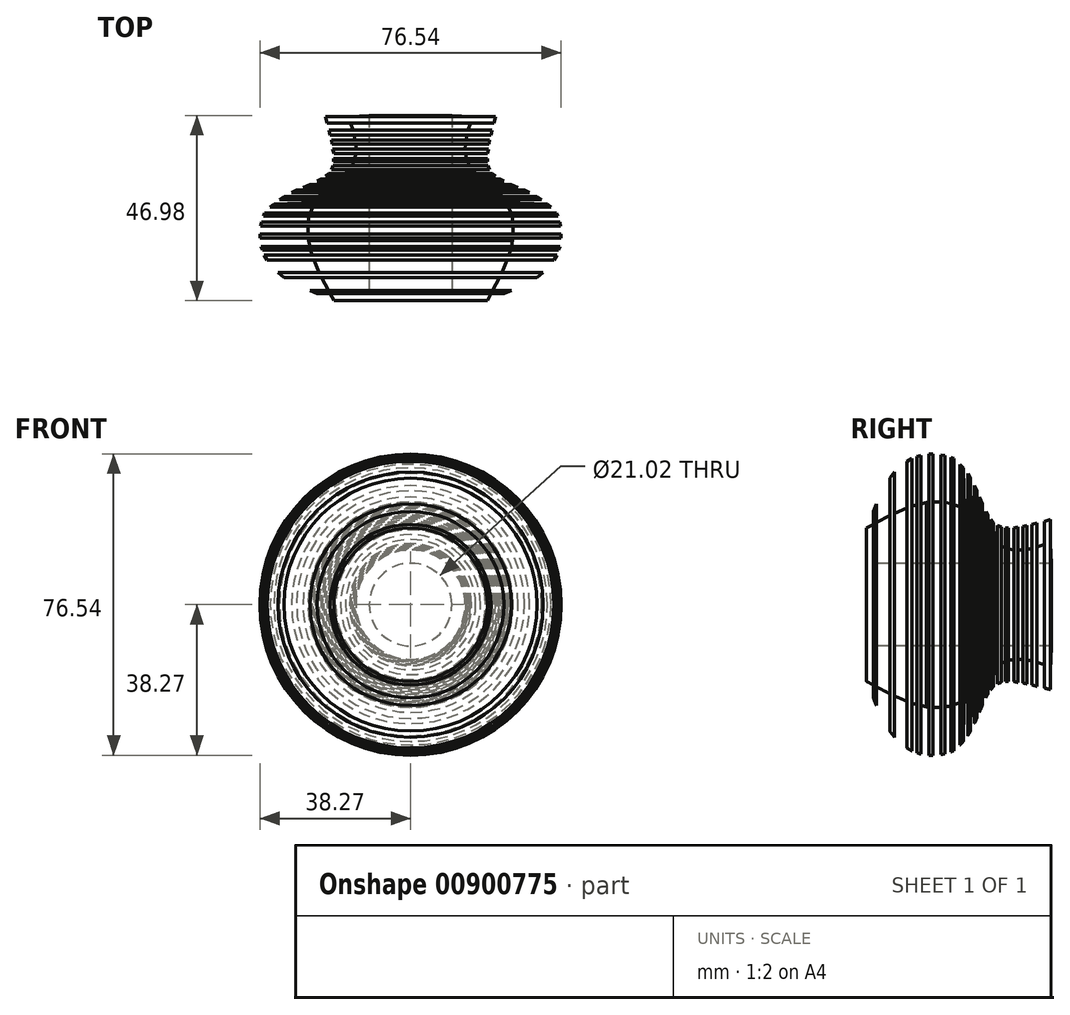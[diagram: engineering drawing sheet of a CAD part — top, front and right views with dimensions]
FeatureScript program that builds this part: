
annotation { "Feature Type Name" : "Feature", "Feature Type Description" : "" }
export const myFeature = defineFeature(function(context is Context, id is Id, definition is map)
    precondition{}
    {
        {
            var Q0;
            Q0=qCreatedBy(makeId("Top.planeOp"),FACE);
            var sketch = newSketch(context, id + "F0", { "sketchPlane" : qUnion([Q0])});
            skLineSegment(sketch, "E0", {"start": v(20.4, 1.74) * mm, "end": v(23.7, 1.74) * mm});
            skLineSegment(sketch, "E1", {"start": v(23.7, 1.74) * mm, "end": v(25.6, 2.49) * mm});
            skLineSegment(sketch, "E2", {"start": v(25.6, 2.49) * mm, "end": v(20.85, 2.49) * mm});
            skLineSegment(sketch, "E3", {"start": v(20.85, 2.49) * mm, "end": v(22.63, 5.9) * mm});
            skLineSegment(sketch, "E4", {"start": v(22.63, 5.9) * mm, "end": v(32.13, 5.9) * mm});
            skLineSegment(sketch, "E5", {"start": v(32.13, 5.9) * mm, "end": v(33.7, 7.16) * mm});
            skLineSegment(sketch, "E6", {"start": v(33.7, 7.16) * mm, "end": v(23.22, 7.16) * mm});
            skLineSegment(sketch, "E7", {"start": v(23.22, 7.16) * mm, "end": v(24.56, 10.32) * mm});
            skLineSegment(sketch, "E8", {"start": v(24.56, 10.32) * mm, "end": v(36.44, 10.32) * mm});
            skLineSegment(sketch, "E9", {"start": v(36.44, 10.32) * mm, "end": v(37.18, 11.5) * mm});
            skLineSegment(sketch, "E10", {"start": v(37.18, 11.5) * mm, "end": v(25, 11.5) * mm});
            skLineSegment(sketch, "E11", {"start": v(25, 11.5) * mm, "end": v(25.42, 12.8) * mm});
            skLineSegment(sketch, "E12", {"start": v(25.42, 12.8) * mm, "end": v(37.62, 12.8) * mm});
            skLineSegment(sketch, "E13", {"start": v(37.62, 12.8) * mm, "end": v(37.94, 13.76) * mm});
            skLineSegment(sketch, "E14", {"start": v(37.94, 13.76) * mm, "end": v(25.6, 13.76) * mm});
            skLineSegment(sketch, "E15", {"start": v(25.6, 13.76) * mm, "end": v(25.96, 15.26) * mm});
            skLineSegment(sketch, "E16", {"start": v(25.96, 15.26) * mm, "end": v(25.96, 15.91) * mm});
            skLineSegment(sketch, "E17", {"start": v(25.96, 15.91) * mm, "end": v(38.27, 15.91) * mm});
            skLineSegment(sketch, "E18", {"start": v(38.27, 15.91) * mm, "end": v(38.27, 16.87) * mm});
            skLineSegment(sketch, "E19", {"start": v(38.27, 16.87) * mm, "end": v(26.08, 16.87) * mm});
            skLineSegment(sketch, "E20", {"start": v(26.08, 16.87) * mm, "end": v(26.08, 18.87) * mm});
            skLineSegment(sketch, "E21", {"start": v(26.08, 18.87) * mm, "end": v(38.09, 18.87) * mm});
            skLineSegment(sketch, "E22", {"start": v(38.09, 19.42) * mm, "end": v(37.9, 19.9) * mm});
            skLineSegment(sketch, "E23", {"start": v(37.9, 19.9) * mm, "end": v(38.09, 18.87) * mm});
            skLineSegment(sketch, "E24", {"start": v(38.07, 19.44) * mm, "end": v(38.07, 19.03) * mm});
            skLineSegment(sketch, "E25", {"start": v(38.07, 19.03) * mm, "end": v(37.9, 19.9) * mm});
            skLineSegment(sketch, "E26", {"start": v(25.98, 19.9) * mm, "end": v(37.9, 19.9) * mm});
            skLineSegment(sketch, "E27", {"start": v(25.98, 19.9) * mm, "end": v(25.74, 21.44) * mm});
            skLineSegment(sketch, "E28", {"start": v(25.74, 21.44) * mm, "end": v(37.4, 21.44) * mm});
            skLineSegment(sketch, "E29", {"start": v(37.4, 21.44) * mm, "end": v(37.08, 22.23) * mm});
            skLineSegment(sketch, "E30", {"start": v(37.08, 22.23) * mm, "end": v(25.45, 22.23) * mm});
            skLineSegment(sketch, "E31", {"start": v(25.45, 22.23) * mm, "end": v(24.77, 23.99) * mm});
            skLineSegment(sketch, "E32", {"start": v(24.77, 23.99) * mm, "end": v(35.66, 23.78) * mm});
            skLineSegment(sketch, "E33", {"start": v(35.66, 23.78) * mm, "end": v(34.74, 24.57) * mm});
            skLineSegment(sketch, "E34", {"start": v(34.74, 24.57) * mm, "end": v(24.32, 24.84) * mm});
            skLineSegment(sketch, "E35", {"start": v(24.32, 24.84) * mm, "end": v(23.7, 25.9) * mm});
            skLineSegment(sketch, "E36", {"start": v(23.7, 25.9) * mm, "end": v(33.28, 25.7) * mm});
            skLineSegment(sketch, "E37", {"start": v(33.28, 25.7) * mm, "end": v(32.16, 26.4) * mm});
            skLineSegment(sketch, "E38", {"start": v(32.16, 26.4) * mm, "end": v(23.23, 26.57) * mm});
            skLineSegment(sketch, "E39", {"start": v(23.23, 26.57) * mm, "end": v(22.44, 27.55) * mm});
            skLineSegment(sketch, "E40", {"start": v(22.44, 27.55) * mm, "end": v(30.23, 27.4) * mm});
            skLineSegment(sketch, "E41", {"start": v(30.23, 27.4) * mm, "end": v(28.93, 28.02) * mm});
            skLineSegment(sketch, "E42", {"start": v(28.93, 28.02) * mm, "end": v(22.05, 28.15) * mm});
            skLineSegment(sketch, "E43", {"start": v(22.05, 28.15) * mm, "end": v(21.24, 28.92) * mm});
            skLineSegment(sketch, "E44", {"start": v(21.24, 28.92) * mm, "end": v(27.35, 28.67) * mm});
            skLineSegment(sketch, "E45", {"start": v(27.35, 28.67) * mm, "end": v(25.54, 29.45) * mm});
            skLineSegment(sketch, "E46", {"start": v(25.54, 29.45) * mm, "end": v(20.56, 29.55) * mm});
            skLineSegment(sketch, "E47", {"start": v(20.56, 29.55) * mm, "end": v(19.53, 30.46) * mm});
            skLineSegment(sketch, "E48", {"start": v(19.53, 30.46) * mm, "end": v(23.7, 30.29) * mm});
            skLineSegment(sketch, "E49", {"start": v(23.7, 30.29) * mm, "end": v(22.75, 30.8) * mm});
            skLineSegment(sketch, "E50", {"start": v(22.75, 30.8) * mm, "end": v(19.03, 30.88) * mm});
            skLineSegment(sketch, "E51", {"start": v(19.03, 30.88) * mm, "end": v(17.78, 31.58) * mm});
            skLineSegment(sketch, "E52", {"start": v(17.78, 31.58) * mm, "end": v(21.62, 31.58) * mm});
            skLineSegment(sketch, "E53", {"start": v(21.62, 31.58) * mm, "end": v(20.85, 32.25) * mm});
            skLineSegment(sketch, "E54", {"start": v(20.85, 32.25) * mm, "end": v(16.53, 32.34) * mm});
            skLineSegment(sketch, "E55", {"start": v(16.53, 32.34) * mm, "end": v(15.5, 33.27) * mm});
            skLineSegment(sketch, "E56", {"start": v(15.5, 33.27) * mm, "end": v(20.1, 33.27) * mm});
            skLineSegment(sketch, "E57", {"start": v(20.1, 33.27) * mm, "end": v(19.72, 34.26) * mm});
            skLineSegment(sketch, "E58", {"start": v(19.72, 34.26) * mm, "end": v(14.92, 34.26) * mm});
            skLineSegment(sketch, "E59", {"start": v(14.92, 34.26) * mm, "end": v(14.42, 35.25) * mm});
            skLineSegment(sketch, "E60", {"start": v(14.42, 35.25) * mm, "end": v(19.55, 35.25) * mm});
            skLineSegment(sketch, "E61", {"start": v(19.55, 35.25) * mm, "end": v(19.55, 36) * mm});
            skLineSegment(sketch, "E62", {"start": v(19.55, 36) * mm, "end": v(14.17, 36) * mm});
            skLineSegment(sketch, "E63", {"start": v(14.17, 36) * mm, "end": v(13.9, 37.4) * mm});
            skLineSegment(sketch, "E64", {"start": v(13.9, 37.4) * mm, "end": v(19.5, 37.4) * mm});
            skLineSegment(sketch, "E65", {"start": v(19.5, 37.4) * mm, "end": v(19.76, 38.5) * mm});
            skLineSegment(sketch, "E66", {"start": v(19.76, 38.5) * mm, "end": v(13.88, 38.5) * mm});
            skLineSegment(sketch, "E67", {"start": v(13.88, 38.5) * mm, "end": v(13.9, 39.75) * mm});
            skLineSegment(sketch, "E68", {"start": v(13.9, 39.75) * mm, "end": v(19.91, 39.75) * mm});
            skLineSegment(sketch, "E69", {"start": v(19.91, 39.75) * mm, "end": v(20.1, 40.81) * mm});
            skLineSegment(sketch, "E70", {"start": v(20.1, 40.81) * mm, "end": v(14.08, 40.81) * mm});
            skLineSegment(sketch, "E71", {"start": v(14.08, 40.81) * mm, "end": v(14.3, 42.04) * mm});
            skLineSegment(sketch, "E72", {"start": v(14.3, 42.04) * mm, "end": v(20.41, 42.04) * mm});
            skLineSegment(sketch, "E73", {"start": v(20.41, 42.04) * mm, "end": v(20.73, 43.27) * mm});
            skLineSegment(sketch, "E74", {"start": v(20.73, 43.27) * mm, "end": v(14.65, 43.27) * mm});
            skLineSegment(sketch, "E75", {"start": v(14.65, 43.27) * mm, "end": v(15.25, 45.15) * mm});
            skLineSegment(sketch, "E76", {"start": v(15.25, 45.15) * mm, "end": v(21.17, 45.15) * mm});
            skLineSegment(sketch, "E77", {"start": v(21.17, 45.15) * mm, "end": v(21.65, 46.98) * mm});
            skLineSegment(sketch, "E78", {"start": v(21.65, 46.98) * mm, "end": v(21.6, 46.77) * mm});
            skLineSegment(sketch, "E79", {"start": v(21.6, 46.77) * mm, "end": v(15.5, 46.77) * mm});
            skLineSegment(sketch, "E80", {"start": v(15.5, 46.77) * mm, "end": v(10.51, 46.98) * mm});
            skLineSegment(sketch, "E81", {"start": v(10.51, 46.98) * mm, "end": v(10.51, 1.74) * mm});
            skLineSegment(sketch, "E82", {"start": v(10.51, 1.74) * mm, "end": v(0, 1.95) * mm});
            skLineSegment(sketch, "E83", {"start": v(0, 1.95) * mm, "end": v(0, 0) * mm});
            skLineSegment(sketch, "E84", {"start": v(0, 0) * mm, "end": v(19.5, 0) * mm});
            skLineSegment(sketch, "E85", {"start": v(19.5, 0) * mm, "end": v(20.4, 1.74) * mm});
            skSolve(sketch);
        }
        {
            var Q0;
            Q0=qCreatedBy(makeId("Top.planeOp"),FACE);
            var sketch = newSketch(context, id + "F1", { "sketchPlane" : qUnion([Q0])});
            skLineSegment(sketch, "E86", {"start": v(0, 0) * mm, "end": v(0, 54.82) * mm});
            skSolve(sketch);
        }
        {
            var Q0;
            Q0=makeQuery(id+"F0.imprint","IMPRINT",FACE,{"disambiguationData":[TD([[makeQuery(id+"F0.imprint","IMPRINT",EDGE,{"derivedFrom":sQuery(id+"F0.wireOp",EDGE,"E0")}),1.0]])]});
            var Q1;
            Q1=sQuery(id+"F1.wireOp",EDGE,"E86");
            revolve(context, id + "F2", {"surfaceOperationType" : NewSurfaceOperationType.NEW, "entities" : qUnion([Q0]), "axis" : qUnion([Q1]), "revolveType" : RevolveType.FULL});
        }
    });
